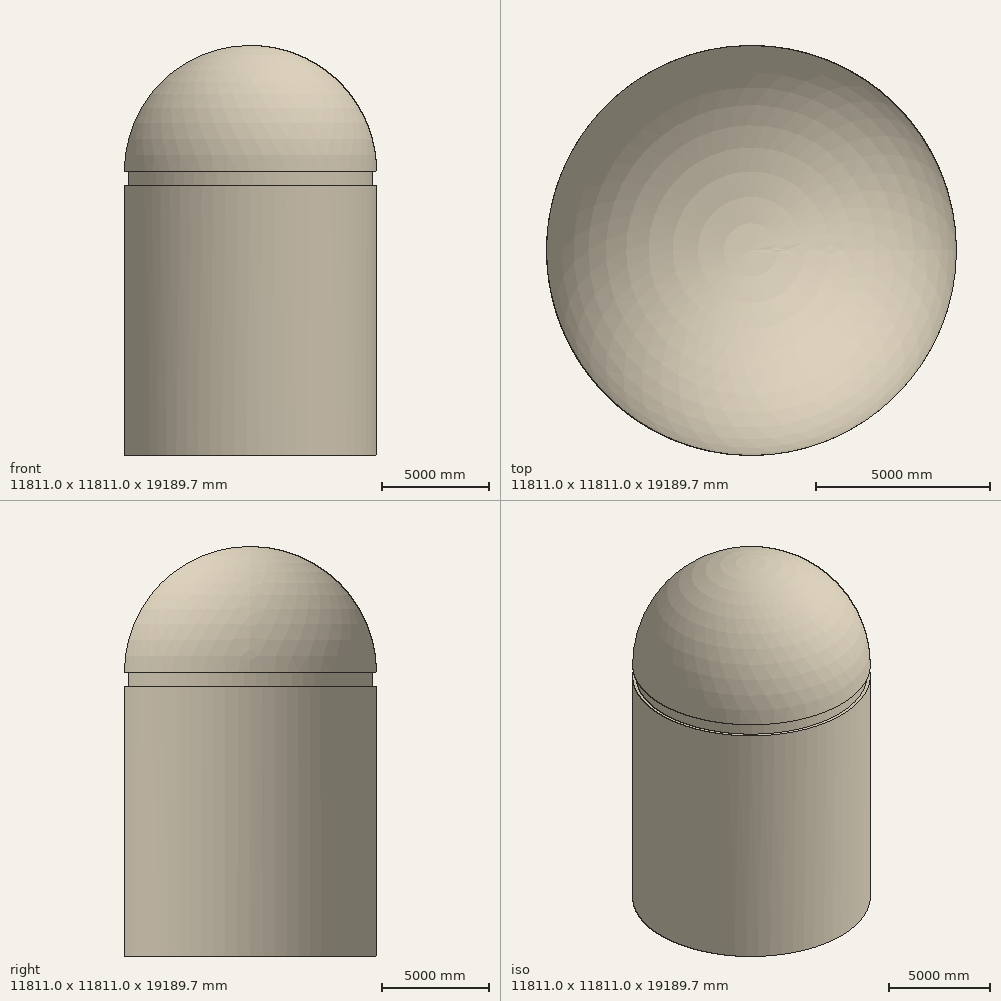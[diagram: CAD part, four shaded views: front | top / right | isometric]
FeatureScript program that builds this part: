
annotation { "Feature Type Name" : "Feature", "Feature Type Description" : "" }
export const myFeature = defineFeature(function(context is Context, id is Id, definition is map)
    precondition{}
    {
        {
            var Q0;
            Q0=qCreatedBy(makeId("Front.planeOp"),FACE);
            var sketch = newSketch(context, id + "F0", { "sketchPlane" : qUnion([Q0])});
            skLineSegment(sketch, "E0", {"start": v(0, 13081.19) * mm, "end": v(5905.5, 13081.19) * mm});
            skLineSegment(sketch, "E1", {"start": v(5905.5, 13081.19) * mm, "end": v(5905.5, 13081.19) * mm});
            skLineSegment(sketch, "E2", {"start": v(0, 18986.69) * mm, "end": v(0, 13081.19) * mm});
            skPoint(sketch, "E3.visualSharp", {"position": v(5905.5, 80.8) * mm});
            skArc(sketch, "E3.filletArc", {"start": v(5905.5, 13081.19) * mm, "mid": v(4175.82, 17257) * mm, "end": v(0, 18986.69) * mm});
            skLineSegment(sketch, "E4", {"start": v(0, 13081.19) * mm, "end": v(0, 12446.19) * mm});
            skLineSegment(sketch, "E5", {"start": v(0, 12446.19) * mm, "end": v(5905.5, 12446.19) * mm});
            skLineSegment(sketch, "E6", {"start": v(5905.5, 12446.19) * mm, "end": v(5905.5, 13081.19) * mm});
            skLineSegment(sketch, "E7.top", {"start": v(0, -203.01) * mm, "end": v(5905.5, -203.01) * mm});
            skLineSegment(sketch, "E7.left", {"start": v(0, 12446.19) * mm, "end": v(0, -203.01) * mm});
            skLineSegment(sketch, "E7.right", {"start": v(5905.5, 12446.19) * mm, "end": v(5905.5, -203.01) * mm});
            skLineSegment(sketch, "E8", {"start": v(5731.96, 13081.19) * mm, "end": v(5731.96, 12446.19) * mm});
            skSolve(sketch);
        }
        {
            var Q0;
            Q0=makeQuery(id+"F0.imprint","IMPRINT",FACE,{"disambiguationData":[TD([[makeQuery(id+"F0.imprint","IMPRINT",EDGE,{"derivedFrom":sQuery(id+"F0.wireOp",EDGE,"E0")}),1.0]])]});
            var Q1;
            Q1=makeQuery(id+"F0.imprint","IMPRINT",FACE,{"disambiguationData":[TD([[makeQuery(id+"F0.imprint","IMPRINT",EDGE,{"derivedFrom":sQuery(id+"F0.wireOp",EDGE,"E0")}),-1.0]])]});
            var Q2;
            Q2=makeQuery(id+"F0.imprint","IMPRINT",FACE,{"disambiguationData":[TD([[makeQuery(id+"F0.imprint","IMPRINT",EDGE,{"derivedFrom":sQuery(id+"F0.wireOp",EDGE,"E5")}),-1.0]])]});
            var Q3;
            Q3=sQuery(id+"F0.wireOp",EDGE,"E7.left");
            revolve(context, id + "F1", {"entities" : qUnion([Q0, Q1, Q2]), "axis" : qUnion([Q3]), "revolveType" : RevolveType.FULL});
        }
        {
            var Q0;
            {var subQ0=sQuery(id+"F0.wireOp",EDGE,"E6");Q0=makeQuery(id+"F0.imprint","IMPRINT",FACE,{"disambiguationData":[TD([[makeQuery(id+"F0.imprint","IMPRINT",EDGE,{"derivedFrom":subQ0}),1.0]])]});}
            var Q1;
            Q1=sQuery(id+"F0.wireOp",EDGE,"E7.left");
            revolve(context, id + "F2", {"operationType" : NewBodyOperationType.REMOVE, "entities" : qUnion([Q0]), "axis" : qUnion([Q1]), "revolveType" : RevolveType.FULL, "oppositeDirection" : true});
        }
    });
